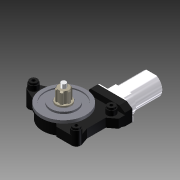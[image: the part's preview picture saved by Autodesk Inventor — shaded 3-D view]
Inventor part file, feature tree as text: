
AUTODESK INVENTOR PART (.ipt)
format: ipt  version: 2014 (Build 180170000, 170)  size: 443,904 bytes
history: native  units: mm
features: extrude x20, sketch x14, plane x4, chamfer x3, projected_geometry x3, pattern_circular x2, revolve x1, hole x1, other x1, fillet x1
ambient origin geometry x8: Origin, YZ Plane, XZ Plane, XY Plane, X Axis, Y Axis, Z Axis, Center Point
bodies: Solid1 (feature_tree)
feature tree (50):
  sketch  "Sketch1"  dims[d0=72.0mm d1=4.8mm d2=0.0mm]
  extrude  "Extrusion1"  Depth=4.8mm TaperAngle=0.0deg
  extrude  "Extrusion2"  Depth=60.0mm
  extrude  "Extrusion3"  Depth=1.9mm TaperAngle=0.0deg
  extrude  "Extrusion4"  Depth=23.8mm
  extrude  "Extrusion5"  Depth=3.0mm
  extrude  "Extrusion6"  Depth=8.0mm
  extrude  "Extrusion7"  Depth=19.9mm
  chamfer  "Chamfer1"  Distance=6.7mm
  pattern_circular  "Circular Pattern1"  Count=6 Angle=360.0deg
  sketch  "Sketch6"  dims[d14=18.0mm d15=0.0mm d16=8.0mm]
  extrude  "Extrusion8"  Depth=14.2mm
  plane  "Work Plane1"
  extrude  "Extrusion9"  Depth=56.76mm
  extrude  "Extrusion10"  Depth=37.0mm
  extrude  "Extrusion11"  Depth=25.0mm
  revolve  "Revolution1"  [1 undecoded]
  extrude  "Extrusion20"  Depth=4.5mm
  pattern_circular  "Circular Pattern2"  [2 undecoded]
  extrude  "Extrusion12"  Depth=15.0mm
  extrude  "Extrusion13"  Depth=4.5mm TaperAngle=0.0deg
  hole  "Hole2"  [1 undecoded]
  plane  "Work Plane4"
  extrude  "Extrusion19"  Depth=17.0mm TaperAngle=0.0deg
  other  "Work Axis1"
  extrude  "Extrusion14"  Depth=14.0mm TaperAngle=0.0deg
  chamfer  "Chamfer2"  Distance=19.5mm
  chamfer  "Chamfer3"  Distance=3.0mm
  fillet  "Fillet1"  Radius=3.0mm
  sketch  "Sketch13"  dims[d31=101.5mm d32=56.76mm]
  extrude  "Extrusion15"  Depth=4.5mm
  extrude  "Extrusion16"  Depth=3.0mm TaperAngle=0.0deg
  extrude  "Extrusion17"  [1 undecoded]
  extrude  "Extrusion18"  Depth=31.0mm
  sketch  "Sketch2"  dims[d3=60.0mm d4=42.0mm]
  sketch  "Sketch3"  dims[d5=25.8mm d6=1.9mm d7=0.0mm]
  sketch  "Sketch4"  dims[d8=1.2mm d9=0.0mm d10=23.8mm]
  sketch  "Sketch5"  dims[d11=3.0mm d12=0.0mm d13=16.4mm]
  sketch  "Sketch7"  dims[d17=6.7mm d18=0.0mm d19=19.9mm]
  sketch  "Sketch10"  dims[d20=4.0mm d21=6.7mm d22=0.0mm]
  projected_geometry  "Projected Loop4"
  sketch  "Sketch11"  dims[d23=1.75mm d24=2.0mm d25=45.0deg d26=60.0mm d27=360.0deg]
  projected_geometry  "Projected Loop5"
  projected_geometry  "Projected Loop6"
  plane  "Work Plane2"
  plane  "Work Plane3"
  sketch  "Sketch12"  dims[d29=68.0mm d30=14.2mm]
  sketch  "Sketch14"  dims[d33=16.3mm d34=37.0mm]
  sketch  "Sketch15"  dims[d35=135.0deg d36=25.0mm]
  sketch  "Sketch16"  dims[d37=10.0mm d38=63.0mm d39=30.5mm d40=13.2mm d41=15.0mm d42=18.6mm d43=0.0mm d44=6.0mm d45=17.0mm d46=0.0mm d47=14.0mm d48=0.0mm d49=19.5mm d50=3.0mm d51=0.0mm d52=3.0mm d53=0.0mm d61=11.9mm d62=3.0mm d63=0.0mm d64=5.0mm d65=6.0mm d66=4.0mm d67=2.0mm d68=90.0deg d69=8.0mm d70=20.594885mm d71=-17.0mm d73=31.0mm d74=12.0mm d75=0.0mm d76=40.0mm d78=6.0mm d79=9.0mm d80=45.0deg d81=6.0mm d82=9.0mm d83=45.0deg d84=6.5mm d85=34.9mm d86=19.95mm d88=3.75mm d89=17.45mm d90=3.0mm d91=10.0mm d92=2.0mm d93=0.0mm d94=15.0mm d95=0.0mm d96=60.0mm d97=0.0mm d98=67.0mm d99=0.0mm d100=0.2mm d101=3.55mm d102=-36.2mm d103=67.0mm d104=0.0mm d106=19.6mm d107=3.8mm d108=90.0deg d109=30.0deg d110=1.0mm d111=19.0mm d112=2.0mm d113=1.0mm d114=4.5mm d115=0.0mm d116=120.0mm d117=360.0deg]
note: 5 required parameter values undecoded (feature->parameter linkage not recoverable at this tier; creation-order binding heuristic only, values carry confidence <= 0.55)